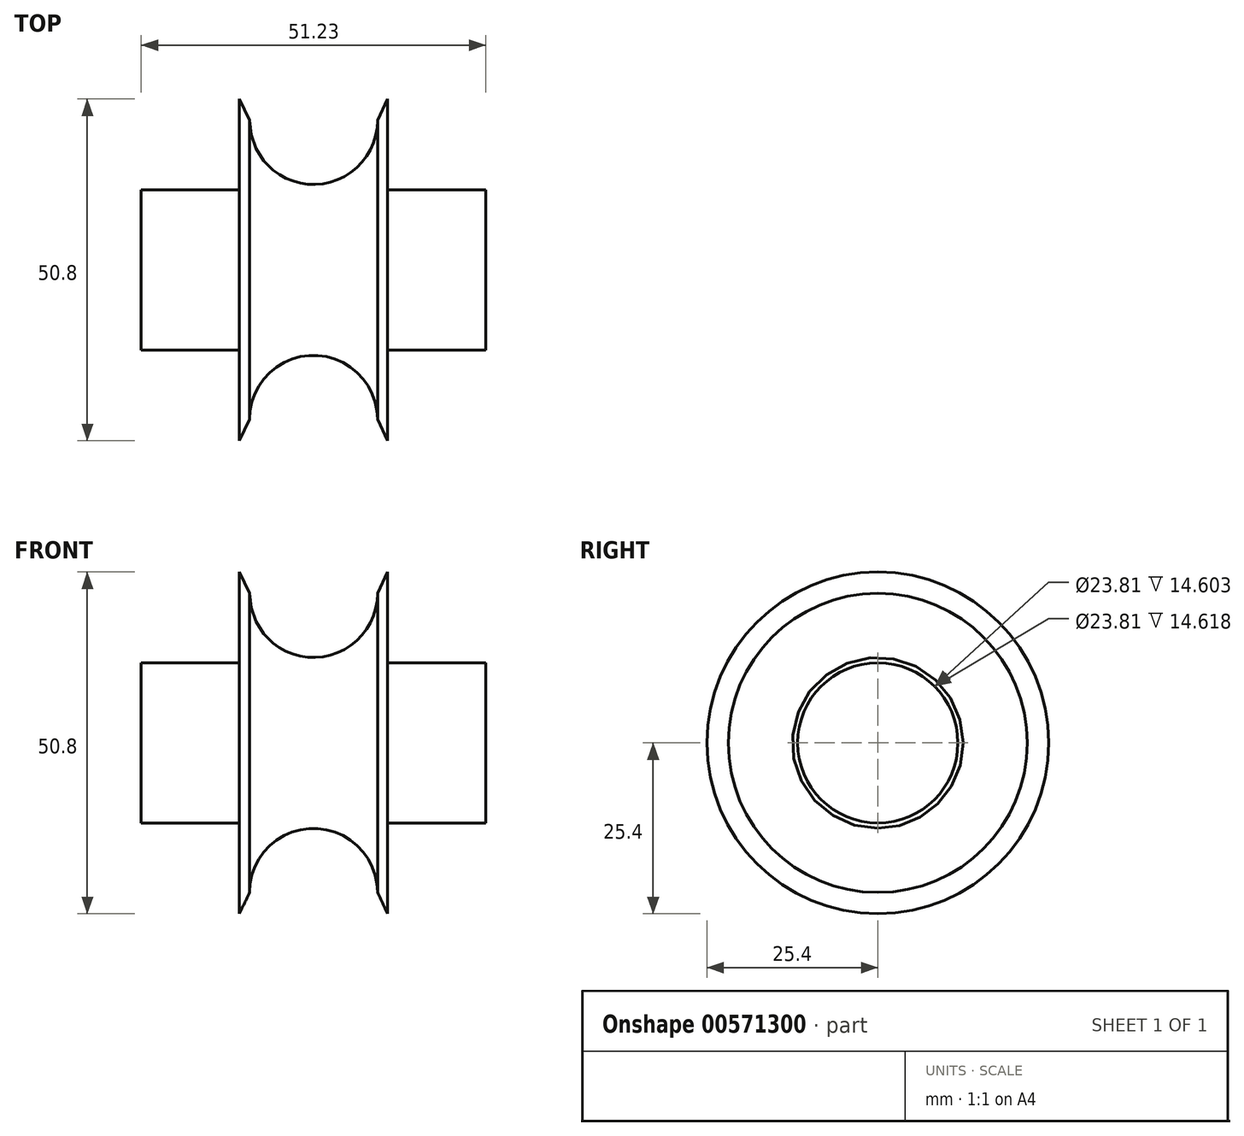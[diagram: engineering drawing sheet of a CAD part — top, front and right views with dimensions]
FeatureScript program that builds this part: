
annotation { "Feature Type Name" : "Feature", "Feature Type Description" : "" }
export const myFeature = defineFeature(function(context is Context, id is Id, definition is map)
    precondition{}
    {
        {
            var Q0;
            Q0=qCreatedBy(makeId("Front.planeOp"),FACE);
            var sketch = newSketch(context, id + "F0", { "sketchPlane" : qUnion([Q0])});
            skLineSegment(sketch, "E0", {"start": v(-65.86, 0) * mm, "end": v(65.86, 0) * mm, "construction": true});
            skLineSegment(sketch, "E1", {"start": v(-12.4, 25.4) * mm, "end": v(-10.92, 22.23) * mm});
            skLineSegment(sketch, "E2", {"start": v(9.61, 25.4) * mm, "end": v(8.13, 22.23) * mm});
            skArc(sketch, "E3", {"start": v(-10.92, 22.23) * mm, "mid": v(-1.4, 12.7) * mm, "end": v(8.13, 22.23) * mm});
            skLineSegment(sketch, "E4", {"start": v(9.61, 11.9) * mm, "end": v(24.23, 11.9) * mm});
            skLineSegment(sketch, "E5", {"start": v(24.23, 11.9) * mm, "end": v(24.23, 0) * mm});
            skLineSegment(sketch, "E6", {"start": v(-12.4, 11.9) * mm, "end": v(-27, 11.9) * mm});
            skLineSegment(sketch, "E7", {"start": v(-27, 11.9) * mm, "end": v(-27, 0) * mm});
            skLineSegment(sketch, "E8", {"start": v(8.13, 32.78) * mm, "end": v(8.13, -34.3) * mm, "construction": true});
            skLineSegment(sketch, "E9", {"start": v(-10.92, 33.68) * mm, "end": v(-10.92, -34.6) * mm, "construction": true});
            skLineSegment(sketch, "E10", {"start": v(9.61, 25.4) * mm, "end": v(9.61, 11.9) * mm});
            skLineSegment(sketch, "E11", {"start": v(9.61, 11.9) * mm, "end": v(9.61, 0) * mm});
            skLineSegment(sketch, "E12", {"start": v(-12.4, 25.4) * mm, "end": v(-12.4, 11.9) * mm});
            skLineSegment(sketch, "E13", {"start": v(-12.4, 11.9) * mm, "end": v(-12.4, 0) * mm});
            skSolve(sketch);
        }
        {
            var Q0;
            Q0 = qSketchRegion(id + "F0", true);
            var Q1;
            Q1=sQuery(id+"F0.wireOp",EDGE,"E12");
            var Q2;
            Q2=sQuery(id+"F0.wireOp",EDGE,"E6");
            var Q3;
            Q3=sQuery(id+"F0.wireOp",EDGE,"E7");
            var Q4;
            Q4=sQuery(id+"F0.wireOp",EDGE,"E4");
            var Q5;
            Q5=sQuery(id+"F0.wireOp",EDGE,"E10");
            var Q6;
            Q6=sQuery(id+"F0.wireOp",EDGE,"E5");
            var Q7;
            Q7=sQuery(id+"F0.wireOp",EDGE,"E3");
            var Q8;
            Q8=sQuery(id+"F0.wireOp",EDGE,"E2");
            var Q9;
            Q9=sQuery(id+"F0.wireOp",EDGE,"E1");
            var Q10;
            Q10=sQuery(id+"F0.wireOp",EDGE,"E0");
            revolve(context, id + "F1", {"bodyType" : ToolBodyType.SURFACE, "entities" : qUnion([Q0]), "surfaceEntities" : qUnion([Q1, Q2, Q3, Q4, Q5, Q6, Q7, Q8, Q9]), "axis" : qUnion([Q10]), "revolveType" : RevolveType.FULL});
        }
    });
